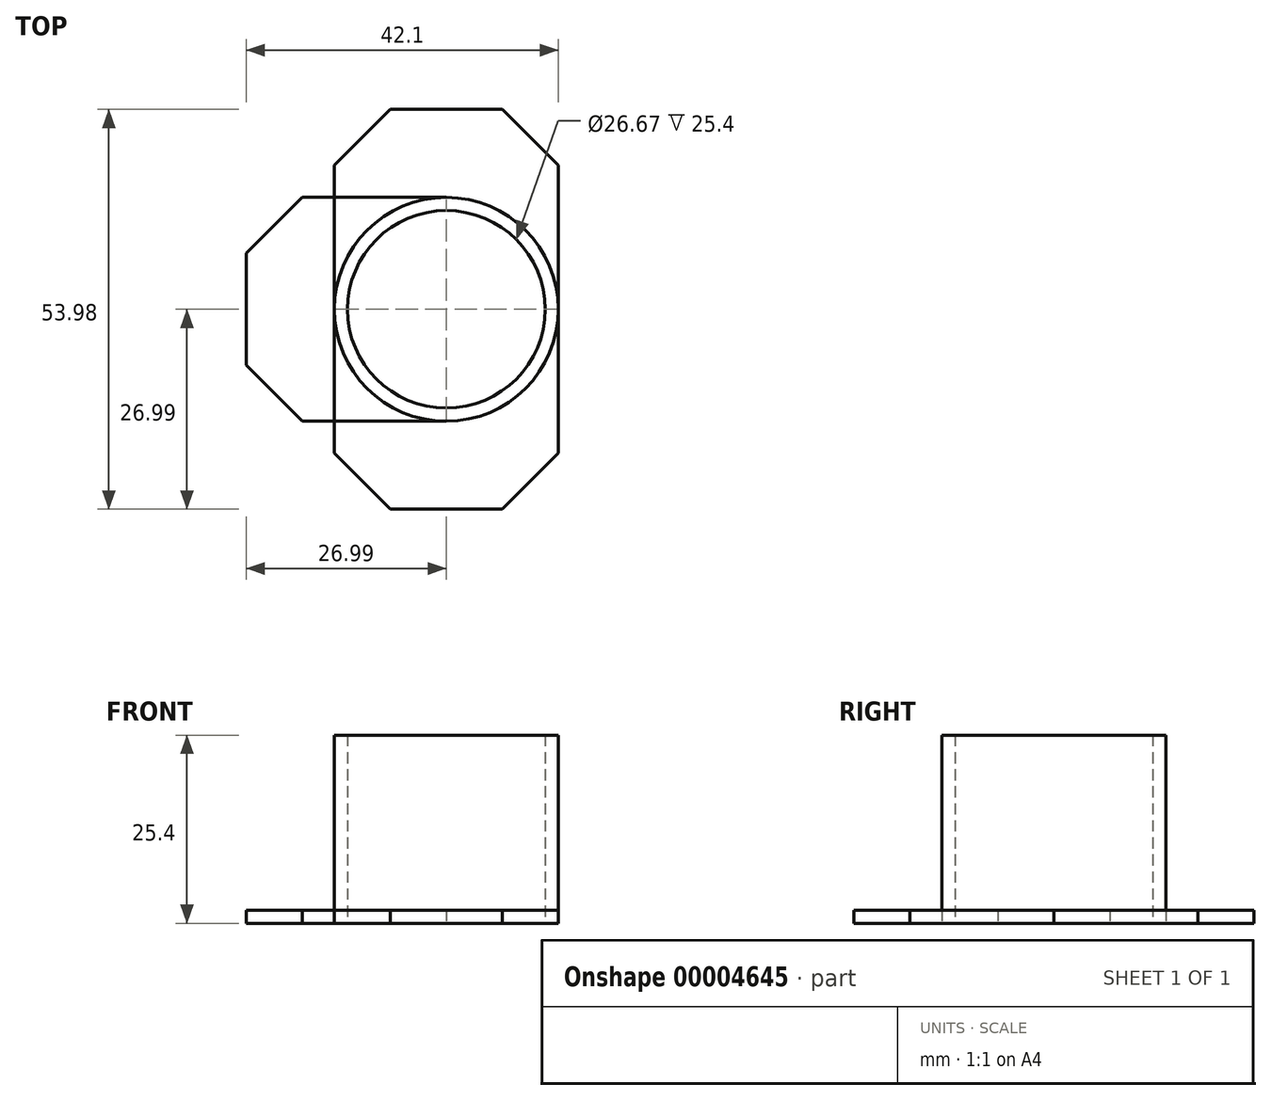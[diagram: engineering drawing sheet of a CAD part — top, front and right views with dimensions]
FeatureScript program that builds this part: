
annotation { "Feature Type Name" : "Feature", "Feature Type Description" : "" }
export const myFeature = defineFeature(function(context is Context, id is Id, definition is map)
    precondition{}
    {
        {
            var Q0;
            Q0=qCreatedBy(makeId("Top.planeOp"),FACE);
            var sketch = newSketch(context, id + "F0", { "sketchPlane" : qUnion([Q0])});
            skCircle(sketch, "E0", {"center": v(0, 0) * mm, "radius": 13.34 * mm});
            skCircle(sketch, "E1.0", {"center": v(0, 0) * mm, "radius": 15.11 * mm});
            skLineSegment(sketch, "E2", {"start": v(-15.11, 0) * mm, "end": v(-15.11, 26.99) * mm});
            skLineSegment(sketch, "E3", {"start": v(15.11, 0) * mm, "end": v(15.11, 26.99) * mm});
            skLineSegment(sketch, "E4", {"start": v(15.11, 26.99) * mm, "end": v(-15.11, 26.99) * mm});
            skLineSegment(sketch, "E5", {"start": v(0, 26.99) * mm, "end": v(15.11, 26.99) * mm});
            skLineSegment(sketch, "E6", {"start": v(-15.11, 26.99) * mm, "end": v(0, 26.99) * mm});
            skLineSegment(sketch, "E7", {"start": v(7.56, 26.99) * mm, "end": v(15.11, 19.43) * mm});
            skLineSegment(sketch, "E8", {"start": v(-7.56, 26.99) * mm, "end": v(-15.11, 19.43) * mm});
            skSolve(sketch);
        }
        {
            var Q0;
            Q0=makeQuery(id+"F0.imprint","IMPRINT",FACE,{"disambiguationData":[TD([[makeQuery(id+"F0.imprint","IMPRINT",EDGE,{"derivedFrom":sQuery(id+"F0.wireOp",EDGE,"E0")}),-1.0]])]});
            extrude(context, id + "F1", {"entities" : qUnion([Q0]), "depth" : 25.4 * mm});
        }
        {
            var Q0;
            {var subQ1=sQuery(id+"F0.wireOp",EDGE,"E7");Q0=makeQuery(id+"F0.imprint","IMPRINT",FACE,{"disambiguationData":[TD([[makeQuery(id+"F0.imprint","IMPRINT",EDGE,{"derivedFrom":subQ1}),-1.0]])]});}
            extrude(context, id + "F2", {"entities" : qUnion([Q0]), "depth" : 1.78 * mm});
        }
        {
            var Q0;
            Q0=qCreatedBy(makeId("Front.planeOp"),FACE);
            var sketch = newSketch(context, id + "F3", { "sketchPlane" : qUnion([Q0])});
            skLineSegment(sketch, "E9", {"start": v(0, 0) * mm, "end": v(0, 45.75) * mm});
            skSolve(sketch);
        }
        {
            var Q0;
            Q0=makeQuery(id+"F2.opExtrude","SWEPT_BODY",BODY,{"disambiguationData":[OSD([sQuery(id+"F0.wireOp",EDGE,"E1.0"),sQuery(id+"F0.wireOp",EDGE,"E2"),sQuery(id+"F0.wireOp",EDGE,"E3"),sQuery(id+"F0.wireOp",EDGE,"E5"),sQuery(id+"F0.wireOp",EDGE,"E7"),sQuery(id+"F0.wireOp",EDGE,"E8")])]});
            var Q1;
            Q1=sQuery(id+"F3.wireOp",EDGE,"E9");
            circularPattern(context, id + "F4", {"entities" : qUnion([Q0]), "axis" : qUnion([Q1]), "angle" : 90 * degree, "instanceCount" : 3});
        }
    });
